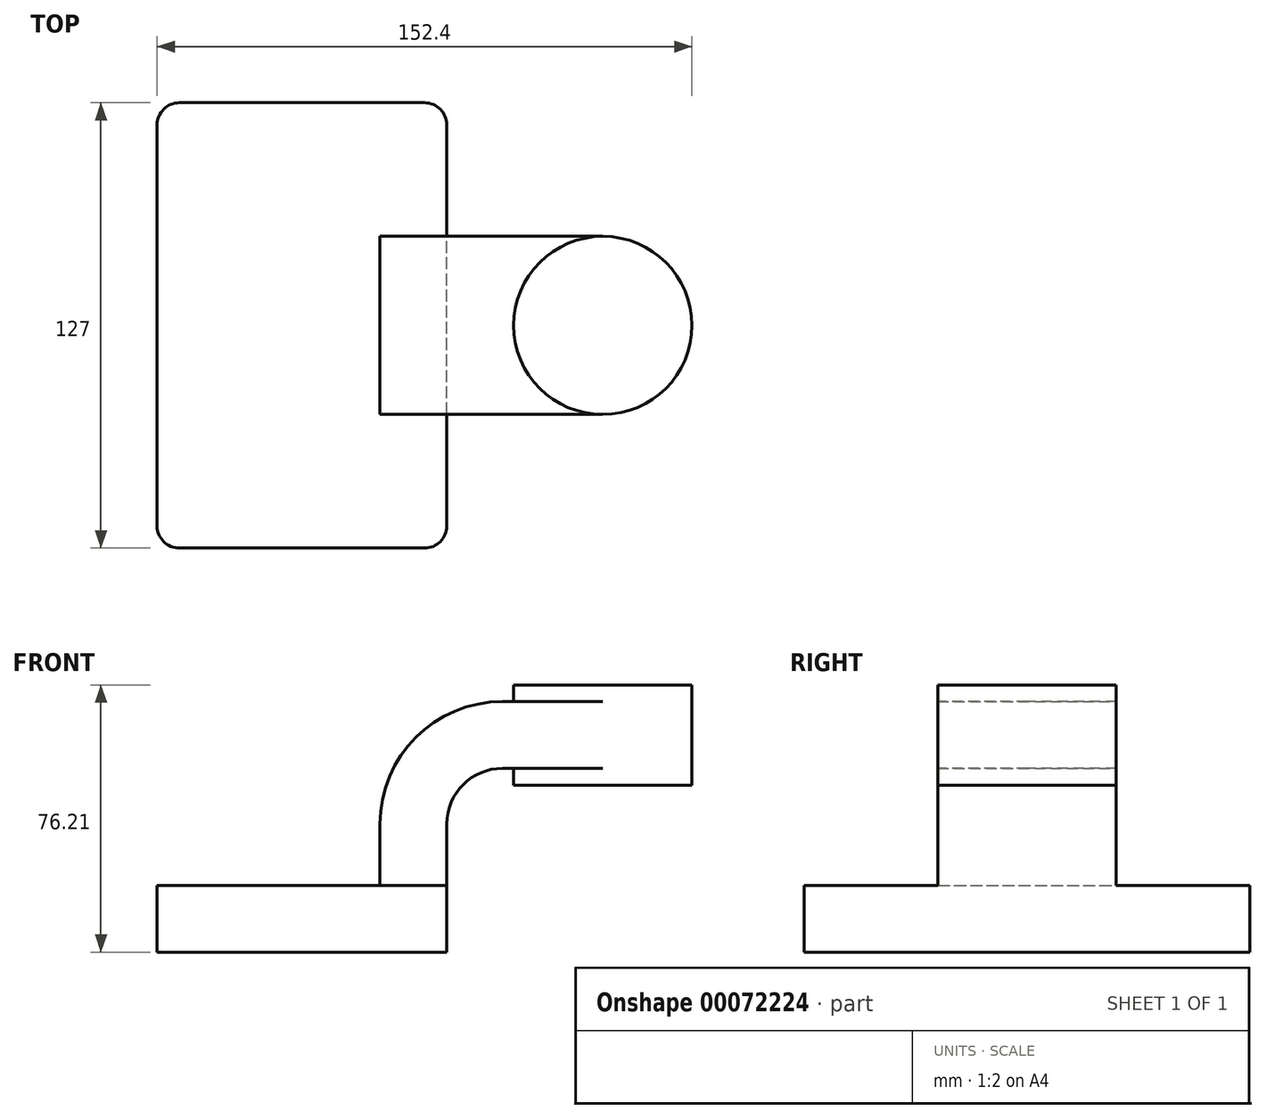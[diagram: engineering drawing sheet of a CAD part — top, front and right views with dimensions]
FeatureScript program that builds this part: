
annotation { "Feature Type Name" : "Feature", "Feature Type Description" : "" }
export const myFeature = defineFeature(function(context is Context, id is Id, definition is map)
    precondition{}
    {
        {
            var Q0;
            Q0=qCreatedBy(makeId("Front.planeOp"),FACE);
            var sketch = newSketch(context, id + "F0", { "sketchPlane" : qUnion([Q0])});
            skLineSegment(sketch, "E0.rect.bottom", {"start": v(41.28, -9.52) * mm, "end": v(-41.28, -9.53) * mm});
            skLineSegment(sketch, "E0.rect.top", {"start": v(41.28, 9.53) * mm, "end": v(-41.28, 9.53) * mm});
            skLineSegment(sketch, "E0.rect.left", {"start": v(41.28, -9.52) * mm, "end": v(41.28, 9.53) * mm});
            skLineSegment(sketch, "E0.rect.right", {"start": v(-41.28, -9.53) * mm, "end": v(-41.28, 9.53) * mm});
            skPoint(sketch, "E0.rect.middle", {"position": v(0, 0) * mm});
            skLineSegment(sketch, "E1.rect.bottom", {"start": v(111.12, 38.1) * mm, "end": v(60.32, 38.1) * mm});
            skLineSegment(sketch, "E1.rect.top", {"start": v(111.12, 66.68) * mm, "end": v(60.32, 66.68) * mm});
            skLineSegment(sketch, "E1.rect.left", {"start": v(111.12, 38.1) * mm, "end": v(111.12, 66.68) * mm});
            skLineSegment(sketch, "E1.rect.right", {"start": v(60.32, 38.1) * mm, "end": v(60.32, 66.68) * mm});
            skPoint(sketch, "E1.rect.middle", {"position": v(85.72, 52.39) * mm});
            skLineSegment(sketch, "E2", {"start": v(41.28, 9.53) * mm, "end": v(41.28, 27) * mm});
            skArc(sketch, "E3", {"start": v(41.27, 27) * mm, "mid": v(45.92, 38.23) * mm, "end": v(57.15, 42.88) * mm});
            skLineSegment(sketch, "E4", {"start": v(57.15, 42.88) * mm, "end": v(85.72, 42.88) * mm});
            skLineSegment(sketch, "E5.0", {"start": v(57.15, 61.93) * mm, "end": v(85.72, 61.93) * mm});
            skArc(sketch, "E5.1", {"start": v(22.23, 27) * mm, "mid": v(32.45, 51.7) * mm, "end": v(57.15, 61.93) * mm});
            skLineSegment(sketch, "E5.2", {"start": v(22.23, 9.53) * mm, "end": v(22.23, 27) * mm});
            skLineSegment(sketch, "E6", {"start": v(85.72, 38.1) * mm, "end": v(85.72, 66.68) * mm});
            skFitSpline(sketch, "E7", {"points": [v(-41.28, 9.53) * mm, v(57.15, 61.93) * mm], "startDerivative": vector(-5, 161.5) * mm, "endDerivative": vector(103.98, -3.1) * mm});
            skSolve(sketch);
        }
        {
            var Q0;
            Q0=makeQuery(id+"F0.imprint","IMPRINT",FACE,{"disambiguationData":[TD([[makeQuery(id+"F0.imprint","IMPRINT",EDGE,{"derivedFrom":sQuery(id+"F0.wireOp",EDGE,"E0.rect.bottom")}),-1.0]])]});
            extrude(context, id + "F1", {"entities" : qUnion([Q0]), "endBound" : BoundingType.SYMMETRIC, "depth" : 127 * mm});
        }
        {
            var Q0;
            {var subQ1=sQuery(id+"F0.wireOp",EDGE,"E2");Q0=makeQuery(id+"F0.imprint","IMPRINT",FACE,{"disambiguationData":[TD([[makeQuery(id+"F0.imprint","IMPRINT",EDGE,{"derivedFrom":subQ1}),1.0]])]});}
            var Q1;
            {var subQ0=sQuery(id+"F0.wireOp",EDGE,"E4");var subQ1=sQuery(id+"F0.wireOp",EDGE,"E1.rect.right");var subQ2=makeQuery(id+"F0.imprint","INTERSECT",VERTEX,{"derivedFrom":[subQ1,subQ0]});Q1=makeQuery(id+"F0.imprint","IMPRINT",FACE,{"disambiguationData":[TD([[makeQuery(id+"F0.imprint","IMPRINT",EDGE,{"disambiguationData":[TD([[subQ2,-1.0]])],"derivedFrom":subQ1}),-1.0]])]});}
            extrude(context, id + "F2", {"entities" : qUnion([Q0, Q1]), "operationType" : NewBodyOperationType.ADD, "endBound" : BoundingType.SYMMETRIC, "depth" : 50.8 * mm});
        }
        {
            var Q0;
            Q0=makeQuery(id+"F0.imprint","IMPRINT",FACE,{"disambiguationData":[TD([[makeQuery(id+"F0.imprint","IMPRINT",EDGE,{"derivedFrom":sQuery(id+"F0.wireOp",EDGE,"E5.1")}),1.0]])]});
            extrude(context, id + "F3", {"entities" : qUnion([Q0]), "operationType" : NewBodyOperationType.ADD, "endBound" : BoundingType.SYMMETRIC, "depth" : 15.88 * mm});
        }
        {
            var Q0;
            {var subQ0=sQuery(id+"F0.wireOp",EDGE,"E1.rect.left");Q0=makeQuery(id+"F0.imprint","IMPRINT",FACE,{"disambiguationData":[TD([[makeQuery(id+"F0.imprint","IMPRINT",EDGE,{"derivedFrom":subQ0}),1.0]])]});}
            var Q1;
            Q1=sQuery(id+"F0.wireOp",EDGE,"E6");
            revolve(context, id + "F4", {"operationType" : NewBodyOperationType.ADD, "entities" : qUnion([Q0]), "axis" : qUnion([Q1]), "revolveType" : RevolveType.FULL});
        }
        {
            var Q0;
            Q0=makeQuery(id+"F1.opExtrude","CAP_EDGE",EDGE,{"disambiguationData":[OSD([sQuery(id+"F0.wireOp",EDGE,"E0.rect.left")])],"isStart":false});
            var Q1;
            Q1=makeQuery(id+"F1.opExtrude","CAP_EDGE",EDGE,{"disambiguationData":[OSD([sQuery(id+"F0.wireOp",EDGE,"E0.rect.right")])],"isStart":false});
            var Q2;
            Q2=makeQuery(id+"F1.opExtrude","CAP_EDGE",EDGE,{"disambiguationData":[OSD([sQuery(id+"F0.wireOp",EDGE,"E0.rect.left")])],"isStart":true});
            var Q3;
            Q3=makeQuery(id+"F1.opExtrude","CAP_EDGE",EDGE,{"disambiguationData":[OSD([sQuery(id+"F0.wireOp",EDGE,"E0.rect.right")])],"isStart":true});
            fillet(context, id + "F5", {"entities" : qUnion([Q0, Q1, Q2, Q3]), "radius" : 6.35 * mm, "tangentPropagation" : true, "allowEdgeOverflow" : false});
        }
    });
